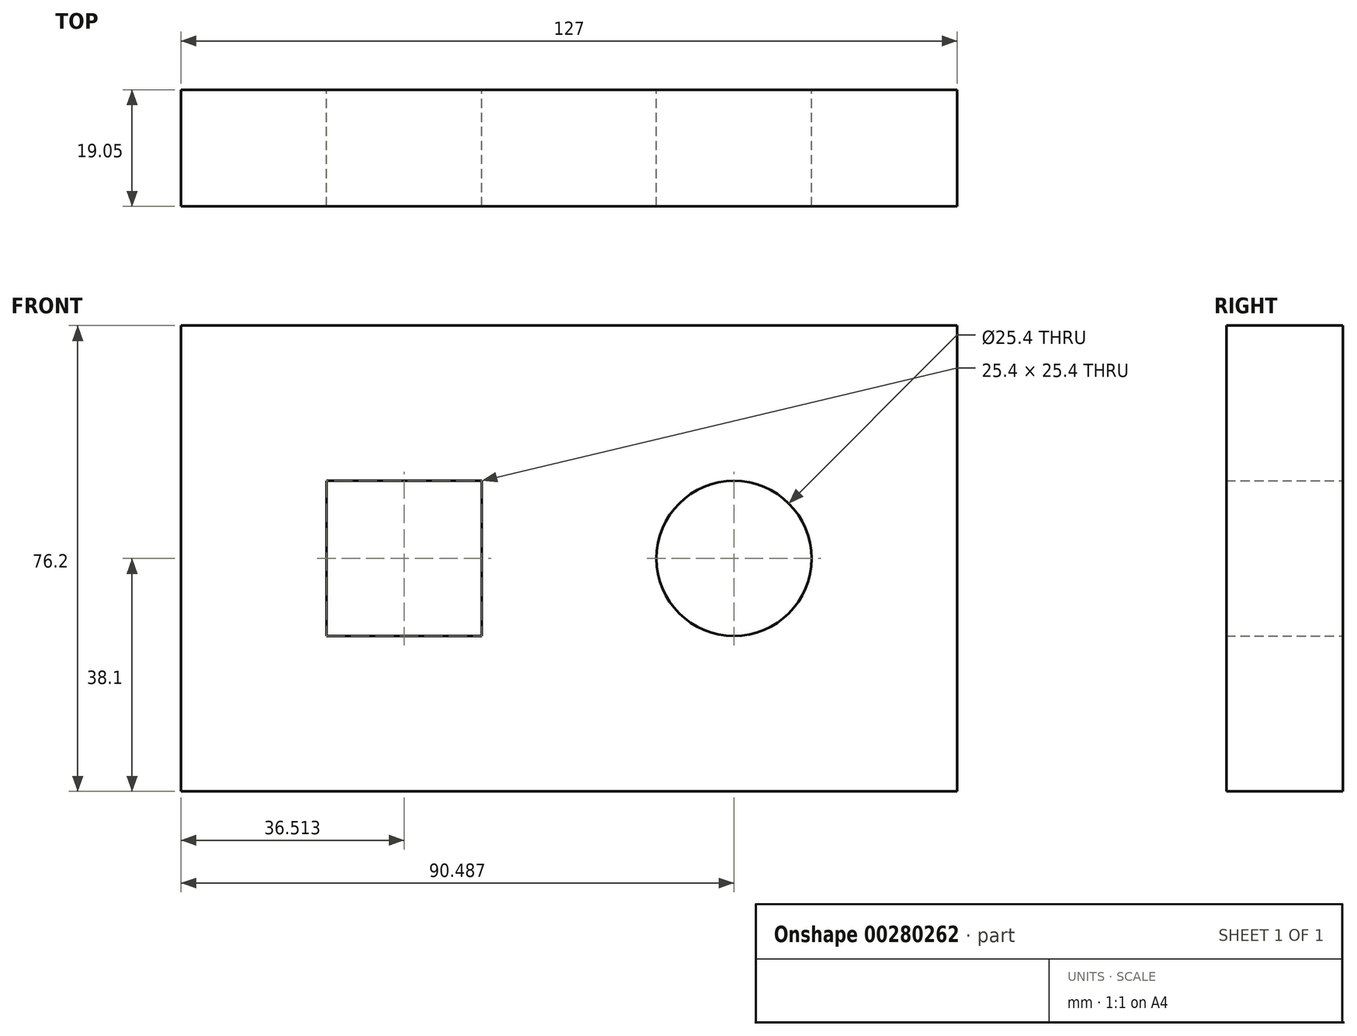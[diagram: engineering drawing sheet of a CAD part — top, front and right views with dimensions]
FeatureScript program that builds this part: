
annotation { "Feature Type Name" : "Feature", "Feature Type Description" : "" }
export const myFeature = defineFeature(function(context is Context, id is Id, definition is map)
    precondition{}
    {
        {
            var Q0;
            Q0=qCreatedBy(makeId("Front.planeOp"),FACE);
            var sketch = newSketch(context, id + "F0", { "sketchPlane" : qUnion([Q0])});
            skLineSegment(sketch, "E0.bottom", {"start": v(0, 0) * mm, "end": v(-127, 0) * mm});
            skLineSegment(sketch, "E0.top", {"start": v(0, 76.2) * mm, "end": v(-127, 76.2) * mm});
            skLineSegment(sketch, "E0.left", {"start": v(0, 0) * mm, "end": v(0, 76.2) * mm});
            skLineSegment(sketch, "E0.right", {"start": v(-127, 0) * mm, "end": v(-127, 76.2) * mm});
            skCircle(sketch, "E1", {"center": v(-36.51, 38.1) * mm, "radius": 12.7 * mm});
            skLineSegment(sketch, "E2.bottom", {"start": v(-103.19, 50.8) * mm, "end": v(-77.79, 50.8) * mm});
            skLineSegment(sketch, "E2.top", {"start": v(-103.19, 25.4) * mm, "end": v(-77.79, 25.4) * mm});
            skLineSegment(sketch, "E2.left", {"start": v(-103.19, 50.8) * mm, "end": v(-103.19, 25.4) * mm});
            skLineSegment(sketch, "E2.right", {"start": v(-77.79, 50.8) * mm, "end": v(-77.79, 25.4) * mm});
            skSolve(sketch);
        }
        {
            var Q0;
            Q0 = qSketchRegion(id + "F0", true);
            extrude(context, id + "F1", {"entities" : qUnion([Q0]), "depth" : 19.05 * mm});
        }
    });
